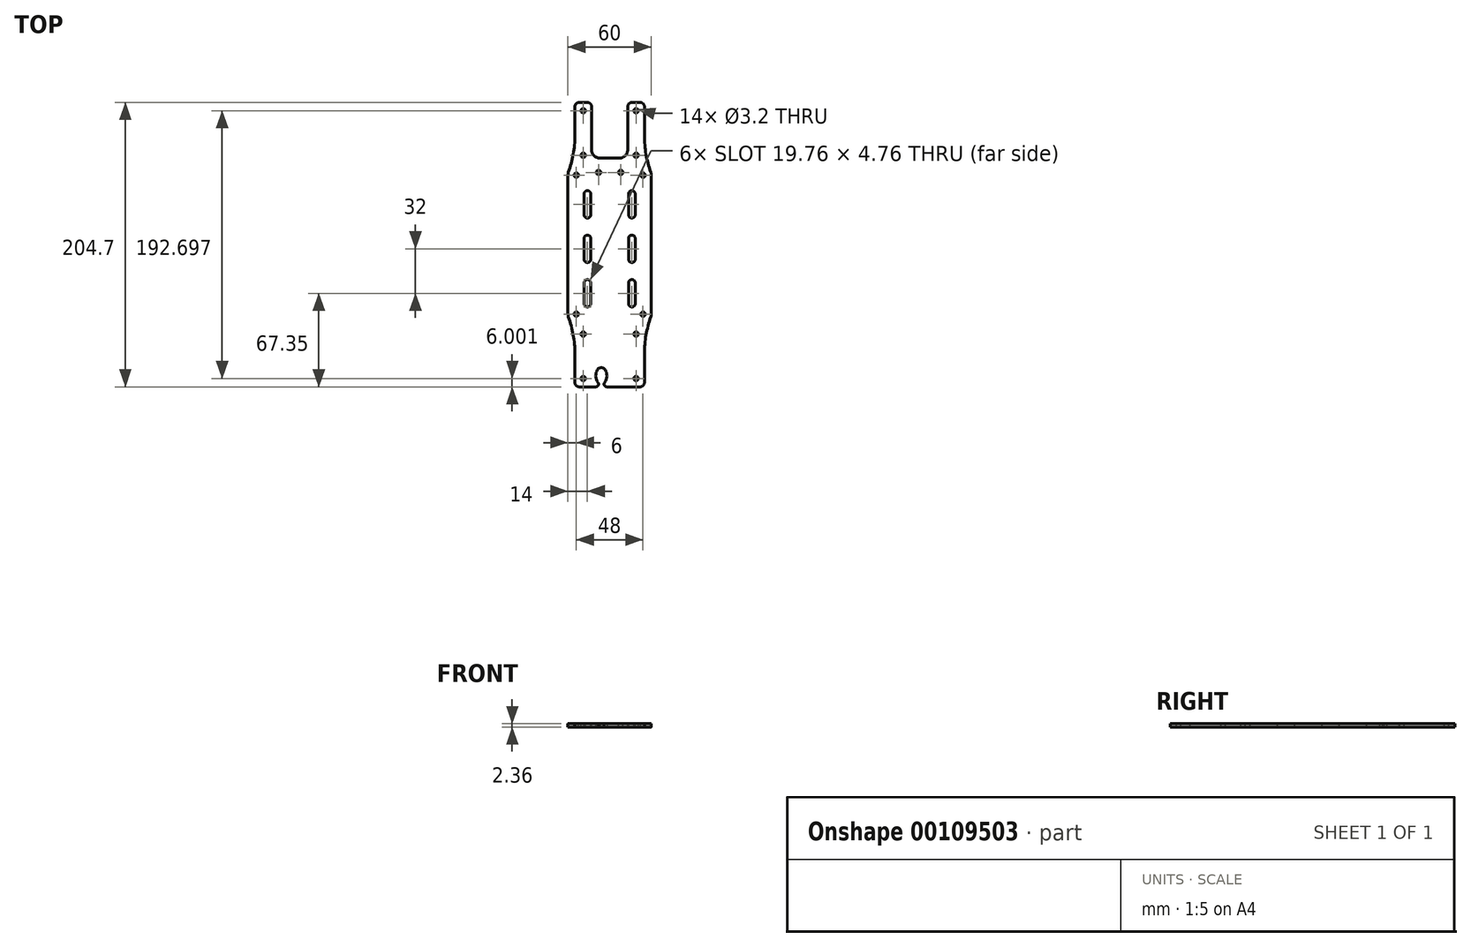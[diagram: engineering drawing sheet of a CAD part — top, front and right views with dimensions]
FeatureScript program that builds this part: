
annotation { "Feature Type Name" : "Feature", "Feature Type Description" : "" }
export const myFeature = defineFeature(function(context is Context, id is Id, definition is map)
    precondition{}
    {
        {
            var Q0;
            Q0=qCreatedBy(makeId("Top.planeOp"),FACE);
            var sketch = newSketch(context, id + "F0", { "sketchPlane" : qUnion([Q0])});
            skLineSegment(sketch, "E0", {"start": v(0, 102.35) * mm, "end": v(-22, 102.35) * mm});
            skLineSegment(sketch, "E1", {"start": v(-25, 99.35) * mm, "end": v(-25, 78.35) * mm});
            skLineSegment(sketch, "E2", {"start": v(-22, -102.35) * mm, "end": v(0, -102.35) * mm});
            skArc(sketch, "E3.filletArc", {"start": v(-22, 102.35) * mm, "mid": v(-24.12, 101.47) * mm, "end": v(-25, 99.35) * mm});
            skArc(sketch, "E4.filletArc", {"start": v(-25, -99.35) * mm, "mid": v(-24.12, -101.47) * mm, "end": v(-22, -102.35) * mm});
            skArc(sketch, "E5.filletArc", {"start": v(-29.64, 52.05) * mm, "mid": v(-29.9, 51.04) * mm, "end": v(-30, 50) * mm});
            skArc(sketch, "E6.MirrorCS", {"start": v(-29.64, -52.05) * mm, "mid": v(-29.9, -51.04) * mm, "end": v(-30, -50) * mm});
            skLineSegment(sketch, "E7.trimOffspring", {"start": v(-25, -78.35) * mm, "end": v(-25, -99.35) * mm});
            skArc(sketch, "E8", {"start": v(-25, -78.35) * mm, "mid": v(-26.17, -65) * mm, "end": v(-29.64, -52.05) * mm});
            skArc(sketch, "E9", {"start": v(-29.64, 52.05) * mm, "mid": v(-26.17, 65) * mm, "end": v(-25, 78.35) * mm});
            skCircle(sketch, "E10", {"center": v(0, 0) * mm, "radius": 125 * mm, "construction": true});
            skLineSegment(sketch, "E11", {"start": v(-95.76, 80.35) * mm, "end": v(95.76, -80.35) * mm, "construction": true});
            skLineSegment(sketch, "E12", {"start": v(95.76, 80.35) * mm, "end": v(-95.76, -80.35) * mm, "construction": true});
            skLineSegment(sketch, "E13", {"start": v(0, 125) * mm, "end": v(0, -125) * mm, "construction": true});
            skLineSegment(sketch, "E14", {"start": v(-95.76, 80.35) * mm, "end": v(95.76, 80.35) * mm, "construction": true});
            skLineSegment(sketch, "E15", {"start": v(-95.76, -80.35) * mm, "end": v(95.76, -80.35) * mm, "construction": true});
            skLineSegment(sketch, "E16", {"start": v(-30, 50) * mm, "end": v(-30, -50) * mm});
            skLineSegment(sketch, "E17.MirrorCS", {"start": v(0, 102.35) * mm, "end": v(22, 102.35) * mm});
            skArc(sketch, "E18.MirrorCS", {"start": v(22, 102.35) * mm, "mid": v(24.12, 101.47) * mm, "end": v(25, 99.35) * mm});
            skLineSegment(sketch, "E19.MirrorCS", {"start": v(25, 99.35) * mm, "end": v(25, 78.35) * mm});
            skArc(sketch, "E20.MirrorCS", {"start": v(29.64, 52.05) * mm, "mid": v(26.17, 65) * mm, "end": v(25, 78.35) * mm});
            skArc(sketch, "E21.MirrorCS", {"start": v(29.64, 52.05) * mm, "mid": v(29.9, 51.04) * mm, "end": v(30, 50) * mm});
            skLineSegment(sketch, "E22.MirrorCS", {"start": v(30, 50) * mm, "end": v(30, -50) * mm});
            skArc(sketch, "E23.MirrorCS", {"start": v(29.64, -52.05) * mm, "mid": v(29.9, -51.04) * mm, "end": v(30, -50) * mm});
            skArc(sketch, "E24.MirrorCS", {"start": v(25, -78.35) * mm, "mid": v(26.17, -65) * mm, "end": v(29.64, -52.05) * mm});
            skArc(sketch, "E25.MirrorCS", {"start": v(25, -99.35) * mm, "mid": v(24.12, -101.47) * mm, "end": v(22, -102.35) * mm});
            skLineSegment(sketch, "E26.MirrorCS", {"start": v(22, -102.35) * mm, "end": v(0, -102.35) * mm});
            skLineSegment(sketch, "E27.MirrorCS", {"start": v(25, -78.35) * mm, "end": v(25, -99.35) * mm});
            skSolve(sketch);
        }
        {
            var Q0;
            Q0=qSketchRegion(id+"F0",true);
            extrude(context, id + "F1", {"entities" : qUnion([Q0]), "oppositeDirection" : true, "depth" : 2.36 * mm});
        }
        {
            var Q0;
            Q0=makeQuery(id+"F1.opExtrude","CAP_FACE",FACE,{"disambiguationData":[OSD([sQuery(id+"F0.wireOp",EDGE,"E0"),sQuery(id+"F0.wireOp",EDGE,"E1"),sQuery(id+"F0.wireOp",EDGE,"E2"),sQuery(id+"F0.wireOp",EDGE,"E3.filletArc"),sQuery(id+"F0.wireOp",EDGE,"E4.filletArc"),sQuery(id+"F0.wireOp",EDGE,"d22b67ea-32aa-4b1a-bfbd-94ae52c1f5b30.MirrorCS"),sQuery(id+"F0.wireOp",EDGE,"d22b67ea-32aa-4b1a-bfbd-94ae52c1f5b31.MirrorCS"),sQuery(id+"F0.wireOp",EDGE,"d22b67ea-32aa-4b1a-bfbd-94ae52c1f5b32.MirrorCS"),sQuery(id+"F0.wireOp",EDGE,"d22b67ea-32aa-4b1a-bfbd-94ae52c1f5b33.MirrorCS"),sQuery(id+"F0.wireOp",EDGE,"d22b67ea-32aa-4b1a-bfbd-94ae52c1f5b34.MirrorCS")])],"isStart":true});
            var sketch = newSketch(context, id + "F2", { "sketchPlane" : qUnion([Q0])});
            skCircle(sketch, "E28", {"center": v(-19, 96.35) * mm, "radius": 1.6 * mm});
            skCircle(sketch, "E29", {"center": v(-19, 64.35) * mm, "radius": 1.6 * mm});
            skCircle(sketch, "E30", {"center": v(-19, -96.35) * mm, "radius": 1.6 * mm});
            skCircle(sketch, "E31", {"center": v(-19, -64.35) * mm, "radius": 1.6 * mm});
            skCircle(sketch, "E32", {"center": v(-24, -50) * mm, "radius": 1.6 * mm});
            skCircle(sketch, "E33", {"center": v(-24, 50) * mm, "radius": 1.6 * mm});
            skLineSegment(sketch, "E34", {"start": v(-19, 96.35) * mm, "end": v(-19, -96.35) * mm, "construction": true});
            skCircle(sketch, "E35.MirrorC", {"center": v(19, 96.35) * mm, "radius": 1.6 * mm});
            skCircle(sketch, "E36.MirrorC", {"center": v(19, 64.35) * mm, "radius": 1.6 * mm});
            skCircle(sketch, "E37.MirrorC", {"center": v(24, 50) * mm, "radius": 1.6 * mm});
            skCircle(sketch, "E38.MirrorC", {"center": v(24, -50) * mm, "radius": 1.6 * mm});
            skCircle(sketch, "E39.MirrorC", {"center": v(19, -64.35) * mm, "radius": 1.6 * mm});
            skCircle(sketch, "E40.MirrorC", {"center": v(19, -96.35) * mm, "radius": 1.6 * mm});
            skLineSegment(sketch, "E41", {"start": v(0, 0) * mm, "end": v(-30, 0) * mm, "construction": true});
            skLineSegment(sketch, "E42.left", {"start": v(-13.62, -42.5) * mm, "end": v(-13.62, -27.5) * mm});
            skLineSegment(sketch, "E42.right", {"start": v(-18.38, -42.5) * mm, "end": v(-18.38, -27.5) * mm});
            skPoint(sketch, "E42.middle", {"position": v(-16, -35) * mm});
            skArc(sketch, "E43", {"start": v(-13.62, -27.5) * mm, "mid": v(-16, -25.12) * mm, "end": v(-18.38, -27.5) * mm});
            skArc(sketch, "E44", {"start": v(-18.38, -42.5) * mm, "mid": v(-16, -44.88) * mm, "end": v(-13.62, -42.5) * mm});
            skArc(sketch, "E45.0.1.0", {"start": v(-18.38, -10.5) * mm, "mid": v(-16, -12.88) * mm, "end": v(-13.62, -10.5) * mm});
            skLineSegment(sketch, "E45.0.1.1", {"start": v(-18.38, -10.5) * mm, "end": v(-18.38, 4.5) * mm});
            skArc(sketch, "E45.0.1.2", {"start": v(-13.62, 4.5) * mm, "mid": v(-16, 6.88) * mm, "end": v(-18.38, 4.5) * mm});
            skLineSegment(sketch, "E45.0.1.3", {"start": v(-13.62, -10.5) * mm, "end": v(-13.62, 4.5) * mm});
            skArc(sketch, "E45.0.2.0", {"start": v(-18.38, 21.5) * mm, "mid": v(-16, 19.12) * mm, "end": v(-13.62, 21.5) * mm});
            skLineSegment(sketch, "E45.0.2.1", {"start": v(-18.38, 21.5) * mm, "end": v(-18.38, 36.5) * mm});
            skArc(sketch, "E45.0.2.2", {"start": v(-13.62, 36.5) * mm, "mid": v(-16, 38.88) * mm, "end": v(-18.38, 36.5) * mm});
            skLineSegment(sketch, "E45.0.2.3", {"start": v(-13.62, 21.5) * mm, "end": v(-13.62, 36.5) * mm});
            skArc(sketch, "E45.1.0.0", {"start": v(13.62, -42.5) * mm, "mid": v(16, -44.88) * mm, "end": v(18.38, -42.5) * mm});
            skLineSegment(sketch, "E45.1.0.1", {"start": v(13.62, -42.5) * mm, "end": v(13.62, -27.5) * mm});
            skArc(sketch, "E45.1.0.2", {"start": v(18.38, -27.5) * mm, "mid": v(16, -25.12) * mm, "end": v(13.62, -27.5) * mm});
            skLineSegment(sketch, "E45.1.0.3", {"start": v(18.38, -42.5) * mm, "end": v(18.38, -27.5) * mm});
            skArc(sketch, "E45.1.1.0", {"start": v(13.62, -10.5) * mm, "mid": v(16, -12.88) * mm, "end": v(18.38, -10.5) * mm});
            skLineSegment(sketch, "E45.1.1.1", {"start": v(13.62, -10.5) * mm, "end": v(13.62, 4.5) * mm});
            skArc(sketch, "E45.1.1.2", {"start": v(18.38, 4.5) * mm, "mid": v(16, 6.88) * mm, "end": v(13.62, 4.5) * mm});
            skLineSegment(sketch, "E45.1.1.3", {"start": v(18.38, -10.5) * mm, "end": v(18.38, 4.5) * mm});
            skArc(sketch, "E45.1.2.0", {"start": v(13.62, 21.5) * mm, "mid": v(16, 19.12) * mm, "end": v(18.38, 21.5) * mm});
            skLineSegment(sketch, "E45.1.2.1", {"start": v(13.62, 21.5) * mm, "end": v(13.62, 36.5) * mm});
            skArc(sketch, "E45.1.2.2", {"start": v(18.38, 36.5) * mm, "mid": v(16, 38.88) * mm, "end": v(13.62, 36.5) * mm});
            skLineSegment(sketch, "E45.1.2.3", {"start": v(18.38, 21.5) * mm, "end": v(18.38, 36.5) * mm});
            skLineSegment(sketch, "E45.direction1", {"start": v(-18.38, -42.5) * mm, "end": v(13.62, -42.5) * mm, "construction": true});
            skLineSegment(sketch, "E45.direction2", {"start": v(-18.38, -42.5) * mm, "end": v(-18.38, -10.5) * mm, "construction": true});
            skLineSegment(sketch, "E46", {"start": v(-8, 52) * mm, "end": v(8, 52) * mm, "construction": true});
            skPoint(sketch, "E47", {"position": v(0, 52) * mm});
            skCircle(sketch, "E48", {"center": v(-8, 52) * mm, "radius": 1.6 * mm});
            skCircle(sketch, "E49", {"center": v(8, 52) * mm, "radius": 1.6 * mm});
            skSolve(sketch);
        }
        {
            var Q0;
            Q0=qSketchRegion(id+"F2",true);
            extrude(context, id + "F3", {"entities" : qUnion([Q0]), "operationType" : NewBodyOperationType.REMOVE, "endBound" : BoundingType.THROUGH_ALL, "oppositeDirection" : true, "depth" : 25.4 * mm});
        }
        {
            var Q0;
            Q0=qCreatedBy(makeId("Top.planeOp"),FACE);
            var sketch = newSketch(context, id + "F4", { "sketchPlane" : qUnion([Q0])});
            skCircle(sketch, "E50.cCircle", {"center": v(-24, 50) * mm, "radius": 3.1 * mm, "construction": true});
            skLineSegment(sketch, "E50.0", {"start": v(-24, 53.58) * mm, "end": v(-20.9, 51.79) * mm, "construction": true});
            skLineSegment(sketch, "E50.1", {"start": v(-20.9, 51.79) * mm, "end": v(-20.9, 48.21) * mm, "construction": true});
            skLineSegment(sketch, "E50.2", {"start": v(-20.9, 48.21) * mm, "end": v(-24, 46.42) * mm, "construction": true});
            skLineSegment(sketch, "E50.3", {"start": v(-24, 46.42) * mm, "end": v(-27.1, 48.21) * mm, "construction": true});
            skLineSegment(sketch, "E50.4", {"start": v(-27.1, 48.21) * mm, "end": v(-27.1, 51.79) * mm, "construction": true});
            skLineSegment(sketch, "E50.5", {"start": v(-27.1, 51.79) * mm, "end": v(-24, 53.58) * mm, "construction": true});
            skPoint(sketch, "E50.0.midPoint", {"position": v(-22.45, 52.68) * mm});
            skArc(sketch, "E51", {"start": v(-20, 45.53) * mm, "mid": v(-24, 56) * mm, "end": v(-28, 45.53) * mm});
            skArc(sketch, "E52", {"start": v(-28, -45.53) * mm, "mid": v(-24, -56) * mm, "end": v(-20, -45.53) * mm});
            skLineSegment(sketch, "E53", {"start": v(-26, 41.06) * mm, "end": v(-26, -41.06) * mm});
            skLineSegment(sketch, "E54", {"start": v(-22, 41.06) * mm, "end": v(-22, -41.06) * mm});
            skPoint(sketch, "E55.visualSharp", {"position": v(-26, 44.34) * mm});
            skArc(sketch, "E55.filletArc", {"start": v(-26, 41.06) * mm, "mid": v(-26.52, 43.5) * mm, "end": v(-28, 45.53) * mm});
            skPoint(sketch, "E56.visualSharp", {"position": v(-22, 44.34) * mm});
            skArc(sketch, "E56.filletArc", {"start": v(-20, 45.53) * mm, "mid": v(-21.48, 43.5) * mm, "end": v(-22, 41.06) * mm});
            skPoint(sketch, "E57.visualSharp", {"position": v(-22, -44.34) * mm});
            skArc(sketch, "E57.filletArc", {"start": v(-22, -41.06) * mm, "mid": v(-21.48, -43.5) * mm, "end": v(-20, -45.53) * mm});
            skPoint(sketch, "E58.visualSharp", {"position": v(-26, -44.34) * mm});
            skArc(sketch, "E58.filletArc", {"start": v(-28, -45.53) * mm, "mid": v(-26.52, -43.5) * mm, "end": v(-26, -41.06) * mm});
            skLineSegment(sketch, "E59", {"start": v(-24, 50) * mm, "end": v(-24, -50) * mm, "construction": true});
            skSolve(sketch);
        }
        {
            var Q0;
            Q0=qSketchRegion(id+"F4",true);
            extrude(context, id + "F5", {"entities" : qUnion([Q0]), "depth" : 25 * mm});
        }
        {
            var Q0;
            Q0=makeQuery(id+"F5.opExtrude","CAP_FACE",FACE,{"disambiguationData":[OSD([sQuery(id+"F4.wireOp",EDGE,"E51"),sQuery(id+"F4.wireOp",EDGE,"E52"),sQuery(id+"F4.wireOp",EDGE,"E53"),sQuery(id+"F4.wireOp",EDGE,"E54"),sQuery(id+"F4.wireOp",EDGE,"E55.filletArc"),sQuery(id+"F4.wireOp",EDGE,"E56.filletArc"),sQuery(id+"F4.wireOp",EDGE,"E57.filletArc"),sQuery(id+"F4.wireOp",EDGE,"E58.filletArc")])],"isStart":true});
            var sketch = newSketch(context, id + "F6", { "sketchPlane" : qUnion([Q0])});
            skCircle(sketch, "E60.cCircle", {"center": v(-24, -50) * mm, "radius": 3.05 * mm, "construction": true});
            skLineSegment(sketch, "E60.0", {"start": v(-27.05, -48.24) * mm, "end": v(-24, -46.48) * mm});
            skLineSegment(sketch, "E60.1", {"start": v(-24, -46.48) * mm, "end": v(-20.95, -48.24) * mm});
            skLineSegment(sketch, "E60.2", {"start": v(-20.95, -48.24) * mm, "end": v(-20.95, -51.76) * mm});
            skLineSegment(sketch, "E60.3", {"start": v(-20.95, -51.76) * mm, "end": v(-24, -53.52) * mm});
            skLineSegment(sketch, "E60.4", {"start": v(-24, -53.52) * mm, "end": v(-27.05, -51.76) * mm});
            skLineSegment(sketch, "E60.5", {"start": v(-27.05, -51.76) * mm, "end": v(-27.05, -48.24) * mm});
            skPoint(sketch, "E60.0.midPoint", {"position": v(-25.53, -47.36) * mm});
            skCircle(sketch, "E61.cCircle", {"center": v(-24, 50) * mm, "radius": 3.05 * mm, "construction": true});
            skLineSegment(sketch, "E61.0", {"start": v(-27.05, 51.76) * mm, "end": v(-24, 53.52) * mm});
            skLineSegment(sketch, "E61.1", {"start": v(-24, 53.52) * mm, "end": v(-20.95, 51.76) * mm});
            skLineSegment(sketch, "E61.2", {"start": v(-20.95, 51.76) * mm, "end": v(-20.95, 48.24) * mm});
            skLineSegment(sketch, "E61.3", {"start": v(-20.95, 48.24) * mm, "end": v(-24, 46.48) * mm});
            skLineSegment(sketch, "E61.4", {"start": v(-24, 46.48) * mm, "end": v(-27.05, 48.24) * mm});
            skLineSegment(sketch, "E61.5", {"start": v(-27.05, 48.24) * mm, "end": v(-27.05, 51.76) * mm});
            skPoint(sketch, "E61.0.midPoint", {"position": v(-25.52, 52.64) * mm});
            skSolve(sketch);
        }
        {
            var Q0;
            Q0=qSketchRegion(id+"F6",true);
            var Q1;
            Q1=makeQuery(id+"F5.opExtrude","CAP_FACE",FACE,{"disambiguationData":[OSD([sQuery(id+"F4.wireOp",EDGE,"E51"),sQuery(id+"F4.wireOp",EDGE,"E52"),sQuery(id+"F4.wireOp",EDGE,"E53"),sQuery(id+"F4.wireOp",EDGE,"E54"),sQuery(id+"F4.wireOp",EDGE,"E55.filletArc"),sQuery(id+"F4.wireOp",EDGE,"E56.filletArc"),sQuery(id+"F4.wireOp",EDGE,"E57.filletArc"),sQuery(id+"F4.wireOp",EDGE,"E58.filletArc")])],"isStart":false});
            extrude(context, id + "F7", {"entities" : qUnion([Q0]), "operationType" : NewBodyOperationType.REMOVE, "endBound" : BoundingType.UP_TO_SURFACE, "oppositeDirection" : true, "endBoundEntityFace" : qUnion([Q1]), "depth" : 25 * mm});
        }
        {
            var Q0;
            Q0=makeQuery(id+"F5.opExtrude","SWEPT_FACE",FACE,{"disambiguationData":[OSD([sQuery(id+"F4.wireOp",EDGE,"E53")])]});
            var sketch = newSketch(context, id + "F8", { "sketchPlane" : qUnion([Q0])});
            skLineSegment(sketch, "E62", {"start": v(-21.13, 12.5) * mm, "end": v(21.13, 12.5) * mm, "construction": true});
            skLineSegment(sketch, "E63.bottom", {"start": v(-11.25, 17.5) * mm, "end": v(-19.25, 17.5) * mm});
            skLineSegment(sketch, "E63.top", {"start": v(-11.25, 7.5) * mm, "end": v(-19.25, 7.5) * mm});
            skLineSegment(sketch, "E63.left", {"start": v(-10.25, 16.5) * mm, "end": v(-10.25, 8.5) * mm});
            skLineSegment(sketch, "E63.right", {"start": v(-20.25, 16.5) * mm, "end": v(-20.25, 8.5) * mm});
            skPoint(sketch, "E63.middle", {"position": v(-15.25, 12.5) * mm});
            skPoint(sketch, "E64.visualSharp", {"position": v(-20.25, 17.5) * mm});
            skArc(sketch, "E64.filletArc", {"start": v(-19.25, 17.5) * mm, "mid": v(-19.96, 17.2) * mm, "end": v(-20.25, 16.5) * mm});
            skPoint(sketch, "E65.visualSharp", {"position": v(-20.25, 7.5) * mm});
            skArc(sketch, "E65.filletArc", {"start": v(-20.25, 8.5) * mm, "mid": v(-19.96, 7.8) * mm, "end": v(-19.25, 7.5) * mm});
            skPoint(sketch, "E66.visualSharp", {"position": v(-10.25, 7.5) * mm});
            skArc(sketch, "E66.filletArc", {"start": v(-11.25, 7.5) * mm, "mid": v(-10.54, 7.8) * mm, "end": v(-10.25, 8.5) * mm});
            skPoint(sketch, "E67.visualSharp", {"position": v(-10.25, 17.5) * mm});
            skArc(sketch, "E67.filletArc", {"start": v(-10.25, 16.5) * mm, "mid": v(-10.54, 17.2) * mm, "end": v(-11.25, 17.5) * mm});
            skLineSegment(sketch, "E68.bottom", {"start": v(-7.5, 0) * mm, "end": v(7.5, 0) * mm});
            skLineSegment(sketch, "E68.top", {"start": v(-6.5, 3.5) * mm, "end": v(6.5, 3.5) * mm});
            skLineSegment(sketch, "E68.left", {"start": v(-7.5, 0) * mm, "end": v(-7.5, 2.5) * mm});
            skLineSegment(sketch, "E68.right", {"start": v(7.5, 0) * mm, "end": v(7.5, 2.5) * mm});
            skPoint(sketch, "E69.visualSharp", {"position": v(-7.5, 3.5) * mm});
            skArc(sketch, "E69.filletArc", {"start": v(-6.5, 3.5) * mm, "mid": v(-7.2, 3.2) * mm, "end": v(-7.5, 2.5) * mm});
            skPoint(sketch, "E70.visualSharp", {"position": v(7.5, 3.5) * mm});
            skArc(sketch, "E70.filletArc", {"start": v(7.5, 2.5) * mm, "mid": v(7.2, 3.2) * mm, "end": v(6.5, 3.5) * mm});
            skArc(sketch, "E71", {"start": v(-27, 25) * mm, "mid": v(-25, 23) * mm, "end": v(-23, 25) * mm});
            skLineSegment(sketch, "E72", {"start": v(-25, 25) * mm, "end": v(-25, 0) * mm, "construction": true});
            skArc(sketch, "E73", {"start": v(-23, 0) * mm, "mid": v(-25, 2) * mm, "end": v(-27, 0) * mm});
            skLineSegment(sketch, "E74", {"start": v(-27, 25) * mm, "end": v(-23, 25) * mm});
            skLineSegment(sketch, "E75", {"start": v(-27, 0) * mm, "end": v(-23, 0) * mm});
            skLineSegment(sketch, "E76", {"start": v(0, 25) * mm, "end": v(0, 0) * mm, "construction": true});
            skPoint(sketch, "E77", {"position": v(0, 12.5) * mm});
            skArc(sketch, "E78.MirrorCS", {"start": v(11.25, 7.5) * mm, "mid": v(10.54, 7.8) * mm, "end": v(10.25, 8.5) * mm});
            skArc(sketch, "E79.MirrorCS", {"start": v(10.25, 16.5) * mm, "mid": v(10.54, 17.2) * mm, "end": v(11.25, 17.5) * mm});
            skArc(sketch, "E80.MirrorCS", {"start": v(20.25, 8.5) * mm, "mid": v(19.96, 7.8) * mm, "end": v(19.25, 7.5) * mm});
            skArc(sketch, "E81.MirrorCS", {"start": v(19.25, 17.5) * mm, "mid": v(19.96, 17.2) * mm, "end": v(20.25, 16.5) * mm});
            skPoint(sketch, "E82.MirrorP", {"position": v(10.25, 17.5) * mm});
            skLineSegment(sketch, "E83.MirrorCS", {"start": v(20.25, 16.5) * mm, "end": v(20.25, 8.5) * mm});
            skLineSegment(sketch, "E84.MirrorCS", {"start": v(10.25, 16.5) * mm, "end": v(10.25, 8.5) * mm});
            skLineSegment(sketch, "E85.MirrorCS", {"start": v(11.25, 17.5) * mm, "end": v(19.25, 17.5) * mm});
            skLineSegment(sketch, "E86.MirrorCS", {"start": v(11.25, 7.5) * mm, "end": v(19.25, 7.5) * mm});
            skPoint(sketch, "E87.MirrorP", {"position": v(20.25, 7.5) * mm});
            skPoint(sketch, "E88.MirrorP", {"position": v(15.25, 12.5) * mm});
            skPoint(sketch, "E89.MirrorP", {"position": v(20.25, 17.5) * mm});
            skPoint(sketch, "E90.MirrorP", {"position": v(10.25, 7.5) * mm});
            skLineSegment(sketch, "E91.MirrorCS", {"start": v(27, 25) * mm, "end": v(23, 25) * mm});
            skLineSegment(sketch, "E92.MirrorCS", {"start": v(25, 25) * mm, "end": v(25, 0) * mm, "construction": true});
            skArc(sketch, "E93.MirrorCS", {"start": v(27, 25) * mm, "mid": v(25, 23) * mm, "end": v(23, 25) * mm});
            skLineSegment(sketch, "E94.MirrorCS", {"start": v(27, 0) * mm, "end": v(23, 0) * mm});
            skArc(sketch, "E95.MirrorCS", {"start": v(23, 0) * mm, "mid": v(25, 2) * mm, "end": v(27, 0) * mm});
            skArc(sketch, "E96.MirrorCS", {"start": v(-6.5, 21.5) * mm, "mid": v(-7.2, 21.8) * mm, "end": v(-7.5, 22.5) * mm});
            skArc(sketch, "E97.MirrorCS", {"start": v(7.5, 22.5) * mm, "mid": v(7.2, 21.8) * mm, "end": v(6.5, 21.5) * mm});
            skPoint(sketch, "E98.MirrorP", {"position": v(-7.5, 21.5) * mm});
            skLineSegment(sketch, "E99.MirrorCS", {"start": v(-6.5, 21.5) * mm, "end": v(6.5, 21.5) * mm});
            skLineSegment(sketch, "E100.MirrorCS", {"start": v(-7.5, 25) * mm, "end": v(-7.5, 22.5) * mm});
            skPoint(sketch, "E101.MirrorP", {"position": v(7.5, 21.5) * mm});
            skLineSegment(sketch, "E102.MirrorCS", {"start": v(7.5, 25) * mm, "end": v(7.5, 22.5) * mm});
            skLineSegment(sketch, "E103.MirrorCS", {"start": v(-7.5, 25) * mm, "end": v(7.5, 25) * mm});
            skSolve(sketch);
        }
        {
            var Q0;
            Q0=qSketchRegion(id+"F8",true);
            var Q1;
            Q1=makeQuery(id+"F5.opExtrude","SWEPT_FACE",FACE,{"disambiguationData":[OSD([sQuery(id+"F4.wireOp",EDGE,"E54")])]});
            extrude(context, id + "F9", {"entities" : qUnion([Q0]), "operationType" : NewBodyOperationType.REMOVE, "endBound" : BoundingType.UP_TO_SURFACE, "oppositeDirection" : true, "endBoundEntityFace" : qUnion([Q1]), "depth" : 25 * mm});
        }
        {
            var Q0;
            Q0=qCreatedBy(makeId("Top.planeOp"),FACE);
            cPlane(context, id + "F10", {"entities" : qUnion([Q0]), "cplaneType" : CPlaneType.OFFSET, "offset" : 12.5 * mm, "width" : 150 * mm, "height" : 150 * mm});
        }
        {
            var Q0;
            Q0=qCreatedBy(id+"F10.planeOp",FACE);
            var sketch = newSketch(context, id + "F11", { "sketchPlane" : qUnion([Q0])});
            skLineSegment(sketch, "E104", {"start": v(-26.25, 21.25) * mm, "end": v(-26.25, 19.75) * mm});
            skLineSegment(sketch, "E105", {"start": v(-25.75, 19.25) * mm, "end": v(-19.25, 19.25) * mm});
            skLineSegment(sketch, "E106", {"start": v(-19.25, 19.25) * mm, "end": v(-18.25, 18.25) * mm});
            skLineSegment(sketch, "E107", {"start": v(-18.25, 18.25) * mm, "end": v(-15.25, 18.25) * mm});
            skLineSegment(sketch, "E108", {"start": v(-6.48, 15.25) * mm, "end": v(-35.06, 15.25) * mm, "construction": true});
            skArc(sketch, "E109", {"start": v(-12.25, 15.25) * mm, "mid": v(-13.13, 17.37) * mm, "end": v(-15.25, 18.25) * mm});
            skLineSegment(sketch, "E110", {"start": v(-26.25, 21.25) * mm, "end": v(-27.75, 21.25) * mm});
            skLineSegment(sketch, "E111", {"start": v(-27.75, 21.25) * mm, "end": v(-27.75, 15.25) * mm});
            skPoint(sketch, "E112.visualSharp", {"position": v(-26.25, 19.25) * mm});
            skArc(sketch, "E112.filletArc", {"start": v(-26.25, 19.75) * mm, "mid": v(-26.1, 19.4) * mm, "end": v(-25.75, 19.25) * mm});
            skLineSegment(sketch, "E113.MirrorCS", {"start": v(-27.75, 9.25) * mm, "end": v(-27.75, 15.25) * mm});
            skLineSegment(sketch, "E114.MirrorCS", {"start": v(-26.25, 9.25) * mm, "end": v(-27.75, 9.25) * mm});
            skLineSegment(sketch, "E115.MirrorCS", {"start": v(-26.25, 9.25) * mm, "end": v(-26.25, 10.75) * mm});
            skArc(sketch, "E116.MirrorCS", {"start": v(-26.25, 10.75) * mm, "mid": v(-26.1, 11.1) * mm, "end": v(-25.75, 11.25) * mm});
            skLineSegment(sketch, "E117.MirrorCS", {"start": v(-25.75, 11.25) * mm, "end": v(-19.25, 11.25) * mm});
            skLineSegment(sketch, "E118.MirrorCS", {"start": v(-19.25, 11.25) * mm, "end": v(-18.25, 12.25) * mm});
            skLineSegment(sketch, "E119.MirrorCS", {"start": v(-18.25, 12.25) * mm, "end": v(-15.25, 12.25) * mm});
            skArc(sketch, "E120.MirrorCS", {"start": v(-12.25, 15.25) * mm, "mid": v(-13.13, 13.13) * mm, "end": v(-15.25, 12.25) * mm});
            skSolve(sketch);
        }
        {
            var Q0;
            Q0=qSketchRegion(id+"F11",true);
            extrude(context, id + "F12", {"entities" : qUnion([Q0]), "endBound" : BoundingType.SYMMETRIC, "depth" : 8 * mm});
        }
        {
            var Q0;
            Q0=makeQuery(id+"F12.opExtrude","CAP_FACE",FACE,{"disambiguationData":[OSD([sQuery(id+"F11.wireOp",EDGE,"E104"),sQuery(id+"F11.wireOp",EDGE,"E105"),sQuery(id+"F11.wireOp",EDGE,"E106"),sQuery(id+"F11.wireOp",EDGE,"E107"),sQuery(id+"F11.wireOp",EDGE,"E109"),sQuery(id+"F11.wireOp",EDGE,"E110"),sQuery(id+"F11.wireOp",EDGE,"E111"),sQuery(id+"F11.wireOp",EDGE,"E112.filletArc"),sQuery(id+"F11.wireOp",EDGE,"E113.MirrorCS"),sQuery(id+"F11.wireOp",EDGE,"E114.MirrorCS"),sQuery(id+"F11.wireOp",EDGE,"E115.MirrorCS"),sQuery(id+"F11.wireOp",EDGE,"E116.MirrorCS"),sQuery(id+"F11.wireOp",EDGE,"E117.MirrorCS"),sQuery(id+"F11.wireOp",EDGE,"E118.MirrorCS"),sQuery(id+"F11.wireOp",EDGE,"E119.MirrorCS"),sQuery(id+"F11.wireOp",EDGE,"E120.MirrorCS")])],"isStart":false});
            var sketch = newSketch(context, id + "F13", { "sketchPlane" : qUnion([Q0])});
            skCircle(sketch, "E121", {"center": v(-15.25, 15.25) * mm, "radius": 1.5 * mm});
            skSolve(sketch);
        }
        {
            var Q0;
            Q0=qSketchRegion(id+"F13",true);
            var Q1;
            Q1=makeQuery(id+"F12.opExtrude","CAP_FACE",FACE,{"disambiguationData":[OSD([sQuery(id+"F11.wireOp",EDGE,"E104"),sQuery(id+"F11.wireOp",EDGE,"E105"),sQuery(id+"F11.wireOp",EDGE,"E106"),sQuery(id+"F11.wireOp",EDGE,"E107"),sQuery(id+"F11.wireOp",EDGE,"E109"),sQuery(id+"F11.wireOp",EDGE,"E110"),sQuery(id+"F11.wireOp",EDGE,"E111"),sQuery(id+"F11.wireOp",EDGE,"E112.filletArc"),sQuery(id+"F11.wireOp",EDGE,"E113.MirrorCS"),sQuery(id+"F11.wireOp",EDGE,"E114.MirrorCS"),sQuery(id+"F11.wireOp",EDGE,"E115.MirrorCS"),sQuery(id+"F11.wireOp",EDGE,"E116.MirrorCS"),sQuery(id+"F11.wireOp",EDGE,"E117.MirrorCS"),sQuery(id+"F11.wireOp",EDGE,"E118.MirrorCS"),sQuery(id+"F11.wireOp",EDGE,"E119.MirrorCS"),sQuery(id+"F11.wireOp",EDGE,"E120.MirrorCS")])],"isStart":true});
            extrude(context, id + "F14", {"entities" : qUnion([Q0]), "operationType" : NewBodyOperationType.REMOVE, "endBound" : BoundingType.UP_TO_SURFACE, "oppositeDirection" : true, "endBoundEntityFace" : qUnion([Q1]), "depth" : 25 * mm});
        }
        {
            var Q0;
            Q0=makeQuery(id+"F5.opExtrude","SWEPT_BODY",BODY,{"disambiguationData":[OSD([sQuery(id+"F4.wireOp",EDGE,"E51"),sQuery(id+"F4.wireOp",EDGE,"E52"),sQuery(id+"F4.wireOp",EDGE,"E53"),sQuery(id+"F4.wireOp",EDGE,"E54"),sQuery(id+"F4.wireOp",EDGE,"E55.filletArc"),sQuery(id+"F4.wireOp",EDGE,"E56.filletArc"),sQuery(id+"F4.wireOp",EDGE,"E57.filletArc"),sQuery(id+"F4.wireOp",EDGE,"E58.filletArc")])]});
            deleteBodies(context, id + "F15", {"entities" : qUnion([Q0])});
        }
        {
            var Q0;
            Q0=makeQuery(id+"F12.opExtrude","SWEPT_BODY",BODY,{"disambiguationData":[OSD([sQuery(id+"F11.wireOp",EDGE,"E104"),sQuery(id+"F11.wireOp",EDGE,"E105"),sQuery(id+"F11.wireOp",EDGE,"E106"),sQuery(id+"F11.wireOp",EDGE,"E107"),sQuery(id+"F11.wireOp",EDGE,"E109"),sQuery(id+"F11.wireOp",EDGE,"E110"),sQuery(id+"F11.wireOp",EDGE,"E111"),sQuery(id+"F11.wireOp",EDGE,"E112.filletArc"),sQuery(id+"F11.wireOp",EDGE,"E113.MirrorCS"),sQuery(id+"F11.wireOp",EDGE,"E114.MirrorCS"),sQuery(id+"F11.wireOp",EDGE,"E115.MirrorCS"),sQuery(id+"F11.wireOp",EDGE,"E116.MirrorCS"),sQuery(id+"F11.wireOp",EDGE,"E117.MirrorCS"),sQuery(id+"F11.wireOp",EDGE,"E118.MirrorCS"),sQuery(id+"F11.wireOp",EDGE,"E119.MirrorCS"),sQuery(id+"F11.wireOp",EDGE,"E120.MirrorCS")])]});
            deleteBodies(context, id + "F16", {"entities" : qUnion([Q0])});
        }
        {
            var Q0;
            Q0=makeQuery(id+"F0.imprint","IMPRINT",FACE,{"disambiguationData":[TD([[makeQuery(id+"F0.imprint","IMPRINT",EDGE,{"derivedFrom":sQuery(id+"F0.wireOp",EDGE,"E0")}),1.0]])]});
            var sketch = newSketch(context, id + "F17", { "sketchPlane" : qUnion([Q0])});
            skLineSegment(sketch, "E122", {"start": v(0, 62.35) * mm, "end": v(-7, 62.35) * mm});
            skLineSegment(sketch, "E123", {"start": v(-13, 68.35) * mm, "end": v(-13, 99.35) * mm});
            skLineSegment(sketch, "E124", {"start": v(-16, 102.35) * mm, "end": v(-16, 102.35) * mm});
            skLineSegment(sketch, "E125", {"start": v(-16, 102.35) * mm, "end": v(-16, 105.35) * mm});
            skLineSegment(sketch, "E126", {"start": v(-16, 105.35) * mm, "end": v(0, 105.35) * mm});
            skPoint(sketch, "E127.visualSharp", {"position": v(-13, 62.35) * mm});
            skArc(sketch, "E127.filletArc", {"start": v(-13, 68.35) * mm, "mid": v(-11.24, 64.1) * mm, "end": v(-7, 62.35) * mm});
            skPoint(sketch, "E128.visualSharp", {"position": v(-13, 102.35) * mm});
            skArc(sketch, "E128.filletArc", {"start": v(-13, 99.35) * mm, "mid": v(-13.88, 101.47) * mm, "end": v(-16, 102.35) * mm});
            skLineSegment(sketch, "E129.MirrorCS", {"start": v(16, 102.35) * mm, "end": v(16, 105.35) * mm});
            skArc(sketch, "E130.MirrorCS", {"start": v(13, 99.35) * mm, "mid": v(13.88, 101.47) * mm, "end": v(16, 102.35) * mm});
            skArc(sketch, "E131.MirrorCS", {"start": v(13, 68.35) * mm, "mid": v(11.24, 64.1) * mm, "end": v(7, 62.35) * mm});
            skPoint(sketch, "E132.MirrorP", {"position": v(13, 102.35) * mm});
            skPoint(sketch, "E133.MirrorP", {"position": v(13, 62.35) * mm});
            skLineSegment(sketch, "E134.MirrorCS", {"start": v(16, 105.35) * mm, "end": v(0, 105.35) * mm});
            skLineSegment(sketch, "E135.MirrorCS", {"start": v(0, 62.35) * mm, "end": v(7, 62.35) * mm});
            skLineSegment(sketch, "E136.MirrorCS", {"start": v(13, 68.35) * mm, "end": v(13, 99.35) * mm});
            skSolve(sketch);
        }
        {
            var Q0;
            Q0=qSketchRegion(id+"F17",true);
            var Q1;
            Q1=makeQuery(id+"F1.opExtrude","CAP_FACE",FACE,{"disambiguationData":[OSD([sQuery(id+"F0.wireOp",EDGE,"E0"),sQuery(id+"F0.wireOp",EDGE,"E1"),sQuery(id+"F0.wireOp",EDGE,"E2"),sQuery(id+"F0.wireOp",EDGE,"E3.filletArc"),sQuery(id+"F0.wireOp",EDGE,"E4.filletArc"),sQuery(id+"F0.wireOp",EDGE,"E5.filletArc"),sQuery(id+"F0.wireOp",EDGE,"E6.MirrorCS"),sQuery(id+"F0.wireOp",EDGE,"E7.trimOffspring"),sQuery(id+"F0.wireOp",EDGE,"E8"),sQuery(id+"F0.wireOp",EDGE,"E9"),sQuery(id+"F0.wireOp",EDGE,"E16"),sQuery(id+"F0.wireOp",EDGE,"E17.MirrorCS"),sQuery(id+"F0.wireOp",EDGE,"E18.MirrorCS"),sQuery(id+"F0.wireOp",EDGE,"E19.MirrorCS"),sQuery(id+"F0.wireOp",EDGE,"E20.MirrorCS"),sQuery(id+"F0.wireOp",EDGE,"E21.MirrorCS"),sQuery(id+"F0.wireOp",EDGE,"E22.MirrorCS"),sQuery(id+"F0.wireOp",EDGE,"E23.MirrorCS"),sQuery(id+"F0.wireOp",EDGE,"E24.MirrorCS"),sQuery(id+"F0.wireOp",EDGE,"E25.MirrorCS"),sQuery(id+"F0.wireOp",EDGE,"E26.MirrorCS"),sQuery(id+"F0.wireOp",EDGE,"E27.MirrorCS")])],"isStart":false});
            extrude(context, id + "F18", {"entities" : qUnion([Q0]), "operationType" : NewBodyOperationType.REMOVE, "endBound" : BoundingType.UP_TO_SURFACE, "oppositeDirection" : true, "endBoundEntityFace" : qUnion([Q1]), "depth" : 25 * mm});
        }
        {
            var Q0;
            Q0=makeQuery(id+"F1.opExtrude","CAP_FACE",FACE,{"disambiguationData":[OSD([sQuery(id+"F0.wireOp",EDGE,"E0"),sQuery(id+"F0.wireOp",EDGE,"E1"),sQuery(id+"F0.wireOp",EDGE,"E2"),sQuery(id+"F0.wireOp",EDGE,"E3.filletArc"),sQuery(id+"F0.wireOp",EDGE,"E4.filletArc"),sQuery(id+"F0.wireOp",EDGE,"E5.filletArc"),sQuery(id+"F0.wireOp",EDGE,"E6.MirrorCS"),sQuery(id+"F0.wireOp",EDGE,"E7.trimOffspring"),sQuery(id+"F0.wireOp",EDGE,"E8"),sQuery(id+"F0.wireOp",EDGE,"E9"),sQuery(id+"F0.wireOp",EDGE,"E16"),sQuery(id+"F0.wireOp",EDGE,"E17.MirrorCS"),sQuery(id+"F0.wireOp",EDGE,"E18.MirrorCS"),sQuery(id+"F0.wireOp",EDGE,"E19.MirrorCS"),sQuery(id+"F0.wireOp",EDGE,"E20.MirrorCS"),sQuery(id+"F0.wireOp",EDGE,"E21.MirrorCS"),sQuery(id+"F0.wireOp",EDGE,"E22.MirrorCS"),sQuery(id+"F0.wireOp",EDGE,"E23.MirrorCS"),sQuery(id+"F0.wireOp",EDGE,"E24.MirrorCS"),sQuery(id+"F0.wireOp",EDGE,"E25.MirrorCS"),sQuery(id+"F0.wireOp",EDGE,"E26.MirrorCS"),sQuery(id+"F0.wireOp",EDGE,"E27.MirrorCS")])],"isStart":true});
            var sketch = newSketch(context, id + "F19", { "sketchPlane" : qUnion([Q0])});
            skEllipticalArc(sketch, "E137", {});
            skArc(sketch, "E138", {"start": v(-10, -102.35) * mm, "mid": v(-8.19, -101.2) * mm, "end": v(-8.48, -99.06) * mm});
            skLineSegment(sketch, "E139", {"start": v(-6, -94.35) * mm, "end": v(-6, -104.97) * mm, "construction": true});
            skArc(sketch, "E140.MirrorCS", {"start": v(-2, -102.35) * mm, "mid": v(-3.81, -101.2) * mm, "end": v(-3.52, -99.06) * mm});
            skLineSegment(sketch, "E141", {"start": v(-10, -102.35) * mm, "end": v(-10, -103.35) * mm});
            skLineSegment(sketch, "E142", {"start": v(-10, -103.35) * mm, "end": v(-2, -103.35) * mm});
            skLineSegment(sketch, "E143", {"start": v(-2, -103.35) * mm, "end": v(-2, -102.35) * mm});
            const initialGuessF19  = {"E137": [-0.006, -0.09434845121081742, 0, 1, 0.006, 0.004, 3.808895997013649, 2.474289310165937]};
            skSetInitialGuess(sketch, initialGuessF19);
            skSolve(sketch);
        }
        {
            var Q0;
            Q0=qSketchRegion(id+"F19",true);
            var Q1;
            Q1=makeQuery(id+"F1.opExtrude","CAP_FACE",FACE,{"disambiguationData":[OSD([sQuery(id+"F0.wireOp",EDGE,"E0"),sQuery(id+"F0.wireOp",EDGE,"E1"),sQuery(id+"F0.wireOp",EDGE,"E2"),sQuery(id+"F0.wireOp",EDGE,"E3.filletArc"),sQuery(id+"F0.wireOp",EDGE,"E4.filletArc"),sQuery(id+"F0.wireOp",EDGE,"E5.filletArc"),sQuery(id+"F0.wireOp",EDGE,"E6.MirrorCS"),sQuery(id+"F0.wireOp",EDGE,"E7.trimOffspring"),sQuery(id+"F0.wireOp",EDGE,"E8"),sQuery(id+"F0.wireOp",EDGE,"E9"),sQuery(id+"F0.wireOp",EDGE,"E16"),sQuery(id+"F0.wireOp",EDGE,"E17.MirrorCS"),sQuery(id+"F0.wireOp",EDGE,"E18.MirrorCS"),sQuery(id+"F0.wireOp",EDGE,"E19.MirrorCS"),sQuery(id+"F0.wireOp",EDGE,"E20.MirrorCS"),sQuery(id+"F0.wireOp",EDGE,"E21.MirrorCS"),sQuery(id+"F0.wireOp",EDGE,"E22.MirrorCS"),sQuery(id+"F0.wireOp",EDGE,"E23.MirrorCS"),sQuery(id+"F0.wireOp",EDGE,"E24.MirrorCS"),sQuery(id+"F0.wireOp",EDGE,"E25.MirrorCS"),sQuery(id+"F0.wireOp",EDGE,"E26.MirrorCS"),sQuery(id+"F0.wireOp",EDGE,"E27.MirrorCS")])],"isStart":false});
            extrude(context, id + "F20", {"entities" : qUnion([Q0]), "operationType" : NewBodyOperationType.REMOVE, "endBound" : BoundingType.UP_TO_SURFACE, "oppositeDirection" : true, "endBoundEntityFace" : qUnion([Q1]), "depth" : 25 * mm});
        }
    });
